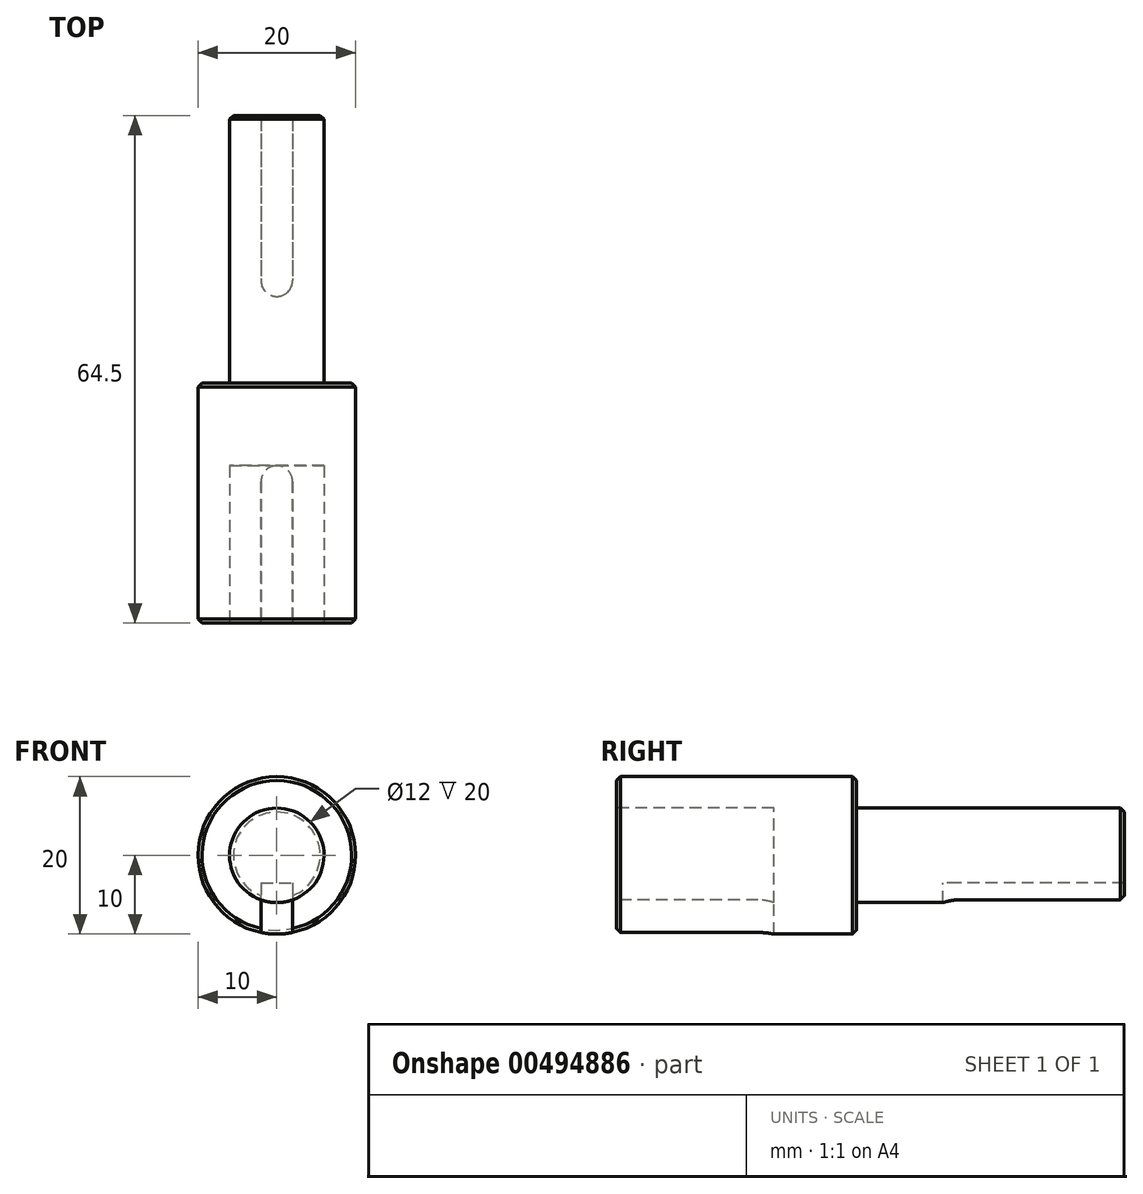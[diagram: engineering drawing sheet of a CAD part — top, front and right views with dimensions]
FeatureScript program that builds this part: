
annotation { "Feature Type Name" : "Feature", "Feature Type Description" : "" }
export const myFeature = defineFeature(function(context is Context, id is Id, definition is map)
    precondition{}
    {
        {
            var Q0;
            Q0=qCreatedBy(makeId("Front.planeOp"),FACE);
            var sketch = newSketch(context, id + "F0", { "sketchPlane" : qUnion([Q0])});
            skCircle(sketch, "E0", {"center": v(0, 0) * mm, "radius": 10 * mm});
            skSolve(sketch);
        }
        {
            var Q0;
            Q0=qSketchRegion(id+"F0",true);
            extrude(context, id + "F1", {"entities" : qUnion([Q0]), "depth" : 30.5 * mm});
        }
        {
            var Q0;
            Q0=makeQuery(id+"F1.opExtrude","CAP_FACE",FACE,{"disambiguationData":[OSD([sQuery(id+"F0.wireOp",EDGE,"E0")])],"isStart":false});
            var sketch = newSketch(context, id + "F2", { "sketchPlane" : qUnion([Q0])});
            skCircle(sketch, "E1", {"center": v(0, 0) * mm, "radius": 6 * mm});
            skSolve(sketch);
        }
        {
            var Q0;
            Q0=qSketchRegion(id+"F2",true);
            extrude(context, id + "F3", {"entities" : qUnion([Q0]), "operationType" : NewBodyOperationType.REMOVE, "oppositeDirection" : true, "depth" : 20 * mm});
        }
        {
            var Q0;
            Q0=makeQuery(id+"F1.opExtrude","CAP_FACE",FACE,{"disambiguationData":[OSD([sQuery(id+"F0.wireOp",EDGE,"E0")])],"isStart":true});
            var sketch = newSketch(context, id + "F4", { "sketchPlane" : qUnion([Q0])});
            skCircle(sketch, "E2", {"center": v(0, 0) * mm, "radius": 6 * mm});
            skSolve(sketch);
        }
        {
            var Q0;
            Q0=qSketchRegion(id+"F4",true);
            extrude(context, id + "F5", {"entities" : qUnion([Q0]), "operationType" : NewBodyOperationType.ADD, "depth" : 34 * mm});
        }
        {
            var Q0;
            Q0=qCreatedBy(makeId("Top.planeOp"),FACE);
            cPlane(context, id + "F6", {"entities" : qUnion([Q0]), "cplaneType" : CPlaneType.OFFSET, "offset" : 6 * mm, "oppositeDirection" : true, "width" : 150 * mm, "height" : 150 * mm});
        }
        {
            var Q0;
            Q0=qCreatedBy(id+"F6.planeOp",FACE);
            var sketch = newSketch(context, id + "F7", { "sketchPlane" : qUnion([Q0])});
            skLineSegment(sketch, "E3.bottom", {"start": v(-2, 34) * mm, "end": v(2, 34) * mm});
            skLineSegment(sketch, "E3.top", {"start": v(-2, 11) * mm, "end": v(2, 11) * mm});
            skLineSegment(sketch, "E3.left", {"start": v(-2, 34) * mm, "end": v(-2, 11) * mm});
            skLineSegment(sketch, "E3.right", {"start": v(2, 34) * mm, "end": v(2, 11) * mm});
            skSolve(sketch);
        }
        {
            var Q0;
            Q0=qSketchRegion(id+"F7",true);
            extrude(context, id + "F8", {"entities" : qUnion([Q0]), "operationType" : NewBodyOperationType.REMOVE, "depth" : 2.5 * mm});
        }
        {
            var Q0;
            Q0=makeQuery(id+"F8.boolean.opBoolean","COPY",EDGE,{"derivedFrom":makeQuery(id+"F8.opExtrude","SWEPT_EDGE",EDGE,{"disambiguationData":[OSD([sQuery(id+"F7.wireOp",EDGE,"E3.top"),sQuery(id+"F7.wireOp",EDGE,"E3.left")])]})});
            var Q1;
            Q1=makeQuery(id+"F8.boolean.opBoolean","COPY",EDGE,{"derivedFrom":makeQuery(id+"F8.opExtrude","SWEPT_EDGE",EDGE,{"disambiguationData":[OSD([sQuery(id+"F7.wireOp",EDGE,"E3.top"),sQuery(id+"F7.wireOp",EDGE,"E3.right")])]})});
            fillet(context, id + "F9", {"entities" : qUnion([Q0, Q1]), "radius" : 2 * mm, "tangentPropagation" : true, "allowEdgeOverflow" : false});
        }
        {
            var Q0;
            Q0=qCreatedBy(makeId("Top.planeOp"),FACE);
            var sketch = newSketch(context, id + "F10", { "sketchPlane" : qUnion([Q0])});
            skLineSegment(sketch, "E4.bottom", {"start": v(-2, -30.5) * mm, "end": v(2, -30.5) * mm});
            skLineSegment(sketch, "E4.top", {"start": v(-2, -10.5) * mm, "end": v(2, -10.5) * mm});
            skLineSegment(sketch, "E4.left", {"start": v(-2, -30.5) * mm, "end": v(-2, -10.5) * mm});
            skLineSegment(sketch, "E4.right", {"start": v(2, -30.5) * mm, "end": v(2, -10.5) * mm});
            skSolve(sketch);
        }
        {
            var Q0;
            Q0=qSketchRegion(id+"F10",true);
            extrude(context, id + "F11", {"entities" : qUnion([Q0]), "operationType" : NewBodyOperationType.REMOVE, "oppositeDirection" : true, "depth" : 25 * mm});
        }
        {
            var Q0;
            Q0=makeQuery(id+"F11.boolean.opBoolean","COPY",EDGE,{"derivedFrom":makeQuery(id+"F11.opExtrude","SWEPT_EDGE",EDGE,{"disambiguationData":[OSD([sQuery(id+"F10.wireOp",EDGE,"E4.top"),sQuery(id+"F10.wireOp",EDGE,"E4.right")])]})});
            var Q1;
            Q1=makeQuery(id+"F11.boolean.opBoolean","COPY",EDGE,{"derivedFrom":makeQuery(id+"F11.opExtrude","SWEPT_EDGE",EDGE,{"disambiguationData":[OSD([sQuery(id+"F10.wireOp",EDGE,"E4.top"),sQuery(id+"F10.wireOp",EDGE,"E4.left")])]})});
            fillet(context, id + "F12", {"entities" : qUnion([Q0, Q1]), "radius" : 2 * mm, "tangentPropagation" : true, "allowEdgeOverflow" : false});
        }
        {
            var Q0;
            Q0=makeQuery(id+"F1.opExtrude","CAP_EDGE",EDGE,{"disambiguationData":[OSD([sQuery(id+"F0.wireOp",EDGE,"E0")])],"isStart":true});
            var Q1;
            Q1=makeQuery(id+"F5.opExtrude","CAP_EDGE",EDGE,{"disambiguationData":[OSD([sQuery(id+"F4.wireOp",EDGE,"E2")])],"isStart":false});
            var Q2;
            Q2=makeQuery(id+"F1.opExtrude","CAP_EDGE",EDGE,{"disambiguationData":[OSD([sQuery(id+"F0.wireOp",EDGE,"E0")])],"isStart":false});
            chamfer(context, id + "F13", {"entities" : qUnion([Q0, Q1, Q2]), "width" : 0.5 * mm, "tangentPropagation" : true});
        }
    });
